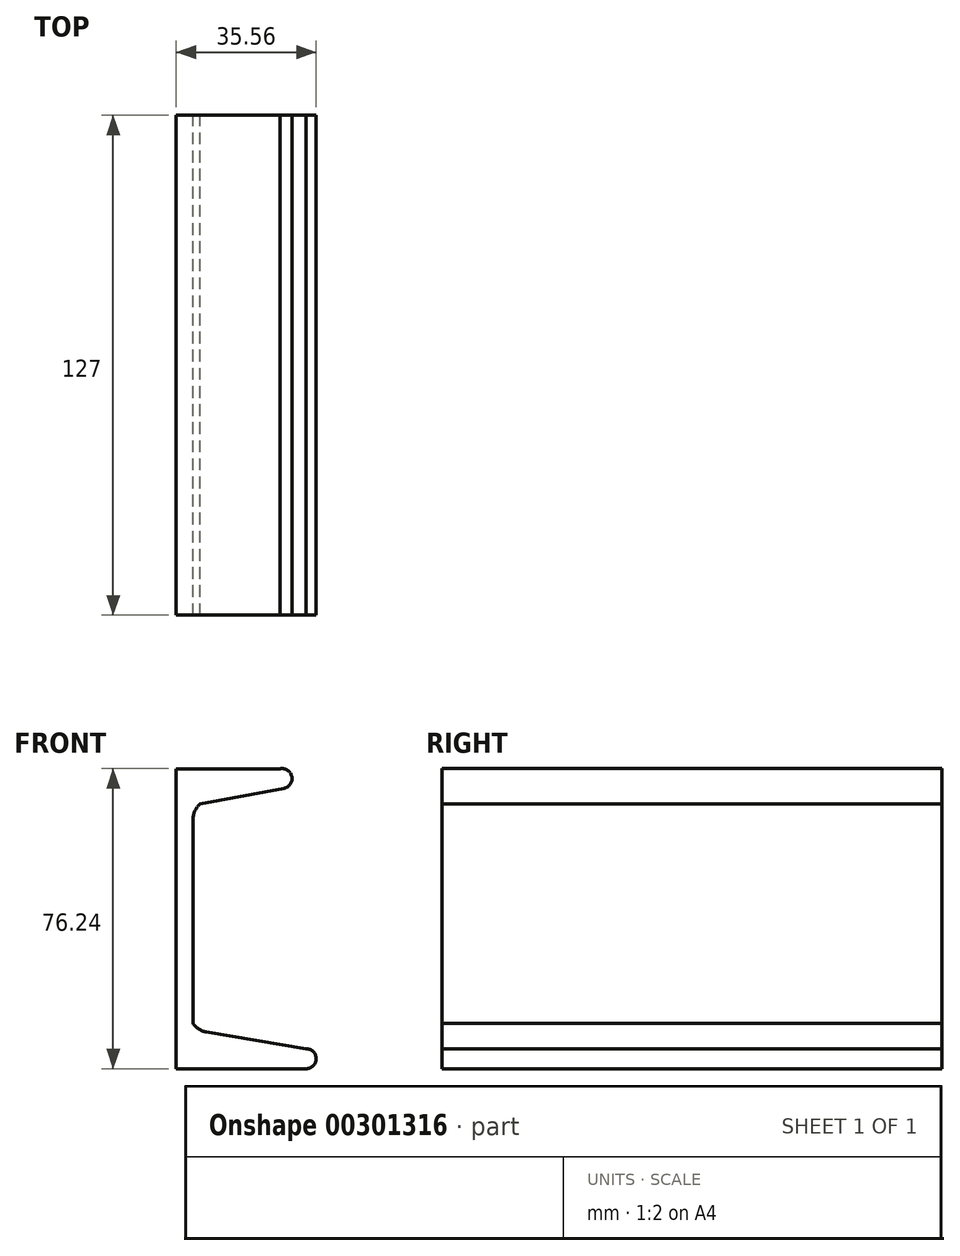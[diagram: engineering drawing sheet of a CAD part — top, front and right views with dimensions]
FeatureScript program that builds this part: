
annotation { "Feature Type Name" : "Feature", "Feature Type Description" : "" }
export const myFeature = defineFeature(function(context is Context, id is Id, definition is map)
    precondition{}
    {
        {
            var Q0;
            Q0=qCreatedBy(makeId("Front.planeOp"),FACE);
            var sketch = newSketch(context, id + "F0", { "sketchPlane" : qUnion([Q0])});
            skLineSegment(sketch, "E0", {"start": v(-38.85, 0) * mm, "end": v(-5.83, 0) * mm});
            skArc(sketch, "E1", {"start": v(-5.83, 0) * mm, "mid": v(-3.3, 2.54) * mm, "end": v(-5.83, 5.08) * mm});
            skLineSegment(sketch, "E2", {"start": v(-5.83, 5.08) * mm, "end": v(-31.27, 9.33) * mm});
            skArc(sketch, "E3", {"start": v(-31.27, 9.33) * mm, "mid": v(-33.13, 10.06) * mm, "end": v(-34.53, 11.46) * mm});
            skLineSegment(sketch, "E4", {"start": v(-34.53, 11.46) * mm, "end": v(-34.53, 63.48) * mm});
            skArc(sketch, "E5", {"start": v(-34.53, 63.48) * mm, "mid": v(-34.07, 65.54) * mm, "end": v(-32.78, 67.22) * mm});
            skLineSegment(sketch, "E6", {"start": v(-32.78, 67.22) * mm, "end": v(-11.5, 71.2) * mm});
            skArc(sketch, "E7", {"start": v(-11.5, 71.2) * mm, "mid": v(-9.47, 74.17) * mm, "end": v(-12.43, 76.2) * mm});
            skLineSegment(sketch, "E8", {"start": v(-12.43, 76.2) * mm, "end": v(-38.85, 76.2) * mm});
            skLineSegment(sketch, "E9", {"start": v(-38.85, 76.2) * mm, "end": v(-38.85, 0) * mm});
            skSolve(sketch);
        }
        {
            var Q0;
            Q0 = qSketchRegion(id + "F0", true);
            extrude(context, id + "F1", {"entities" : qUnion([Q0]), "endBound" : BoundingType.SYMMETRIC, "depth" : 127 * mm});
        }
    });
